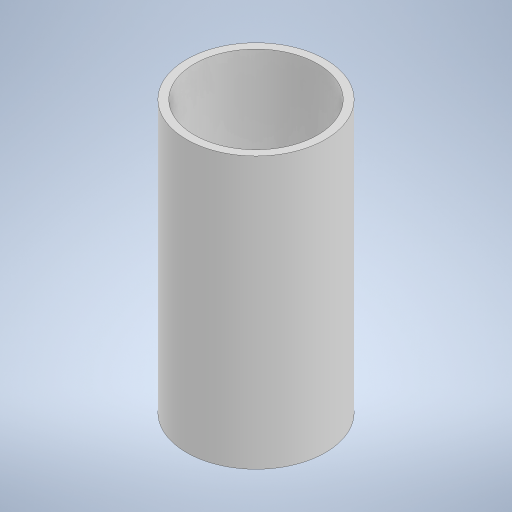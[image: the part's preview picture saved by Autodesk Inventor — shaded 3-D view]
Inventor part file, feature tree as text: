
AUTODESK INVENTOR PART (.ipt)
format: ipt  version: 2023 (Build 270158000, 158)  size: 208,384 bytes
history: native  units: in
note: dims shown in document units (in); Inventor stores cm internally (conversion verified against a paired STEP export)
features: extrude x1, sketch x1
ambient origin geometry x8: Origin, YZ Plane, XZ Plane, XY Plane, X Axis, Y Axis, Z Axis, Center Point
bodies: Solid1 (feature_tree)
feature tree (2):
  extrude  "Extrusion1"  Depth=0.55in
  sketch  "Sketch1"  dims[d0=0.2812in d1=0.25in d2=0.55in d3=0.0in]
